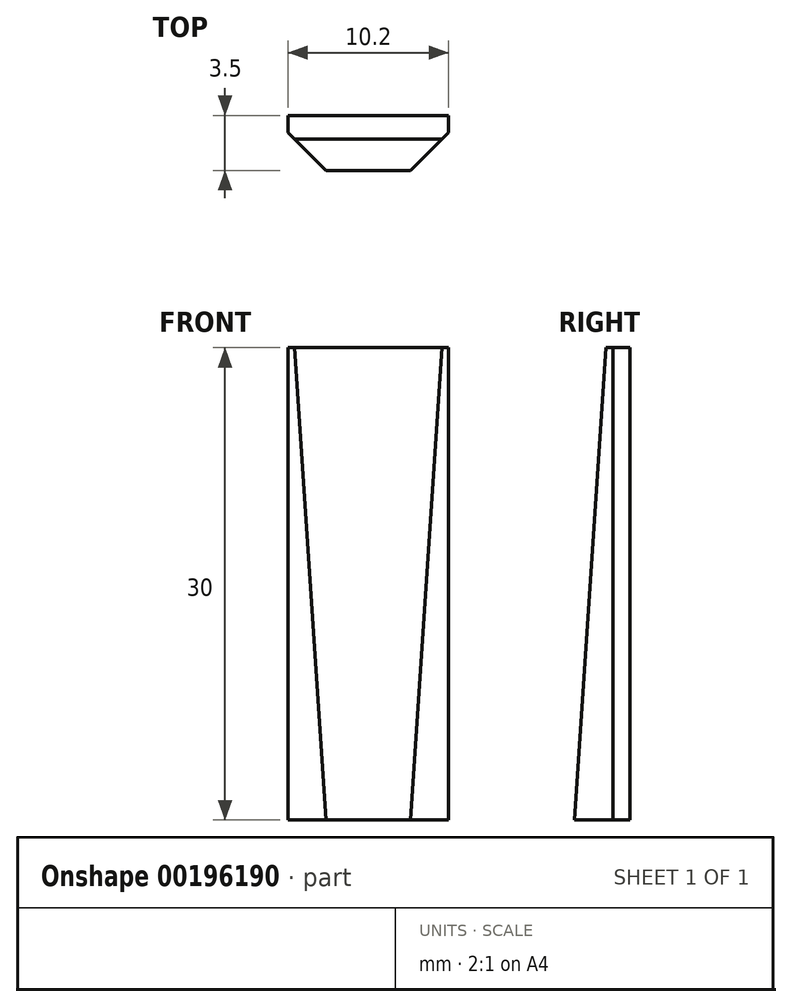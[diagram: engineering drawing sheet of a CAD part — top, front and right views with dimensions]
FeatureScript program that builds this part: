
annotation { "Feature Type Name" : "Feature", "Feature Type Description" : "" }
export const myFeature = defineFeature(function(context is Context, id is Id, definition is map)
    precondition{}
    {
        {
            var Q0;
            Q0=qCreatedBy(makeId("Top.planeOp"),FACE);
            var sketch = newSketch(context, id + "F0", { "sketchPlane" : qUnion([Q0])});
            skLineSegment(sketch, "E0", {"start": v(-11, -1.64) * mm, "end": v(-11, 0) * mm, "construction": true});
            skLineSegment(sketch, "E1", {"start": v(-11, -1.64) * mm, "end": v(-8.34, -4.3) * mm, "construction": true});
            skLineSegment(sketch, "E2", {"start": v(-2.66, -4.3) * mm, "end": v(0, -1.64) * mm, "construction": true});
            skLineSegment(sketch, "E3", {"start": v(0, 0) * mm, "end": v(0, -1.64) * mm, "construction": true});
            skLineSegment(sketch, "E4", {"start": v(-11, 0) * mm, "end": v(0, 0) * mm, "construction": true});
            skLineSegment(sketch, "E5", {"start": v(-2.66, -4.3) * mm, "end": v(-8.34, -4.3) * mm, "construction": true});
            skLineSegment(sketch, "E6.0", {"start": v(-10.6, -1.47) * mm, "end": v(-10.6, -0.4) * mm});
            skLineSegment(sketch, "E6.1", {"start": v(-0.4, -0.4) * mm, "end": v(-0.4, -1.47) * mm});
            skLineSegment(sketch, "E6.2", {"start": v(-2.83, -3.9) * mm, "end": v(-0.4, -1.47) * mm});
            skLineSegment(sketch, "E6.3", {"start": v(-10.6, -0.4) * mm, "end": v(-0.4, -0.4) * mm});
            skLineSegment(sketch, "E6.4", {"start": v(-2.83, -3.9) * mm, "end": v(-8.17, -3.9) * mm});
            skLineSegment(sketch, "E6.5", {"start": v(-10.6, -1.47) * mm, "end": v(-8.17, -3.9) * mm});
            skSolve(sketch);
        }
        {
            var Q0;
            Q0=makeQuery(id+"F0.imprint","IMPRINT",FACE,{"disambiguationData":[TD([[makeQuery(id+"F0.imprint","IMPRINT",EDGE,{"derivedFrom":sQuery(id+"F0.wireOp",EDGE,"E6.0")}),-1.0]])]});
            extrude(context, id + "F1", {"entities" : qUnion([Q0]), "depth" : 30 * mm});
        }
        {
            var Q0;
            Q0=makeQuery(id+"F1.opExtrude","CAP_EDGE",EDGE,{"disambiguationData":[OSD([sQuery(id+"F0.wireOp",EDGE,"E6.4")])],"isStart":false});
            chamfer(context, id + "F2", {"entities" : qUnion([Q0]), "chamferType" : ChamferType.TWO_OFFSETS, "width1" : 30 * mm, "oppositeDirection" : false, "width2" : 2 * mm, "tangentPropagation" : true});
        }
    });
